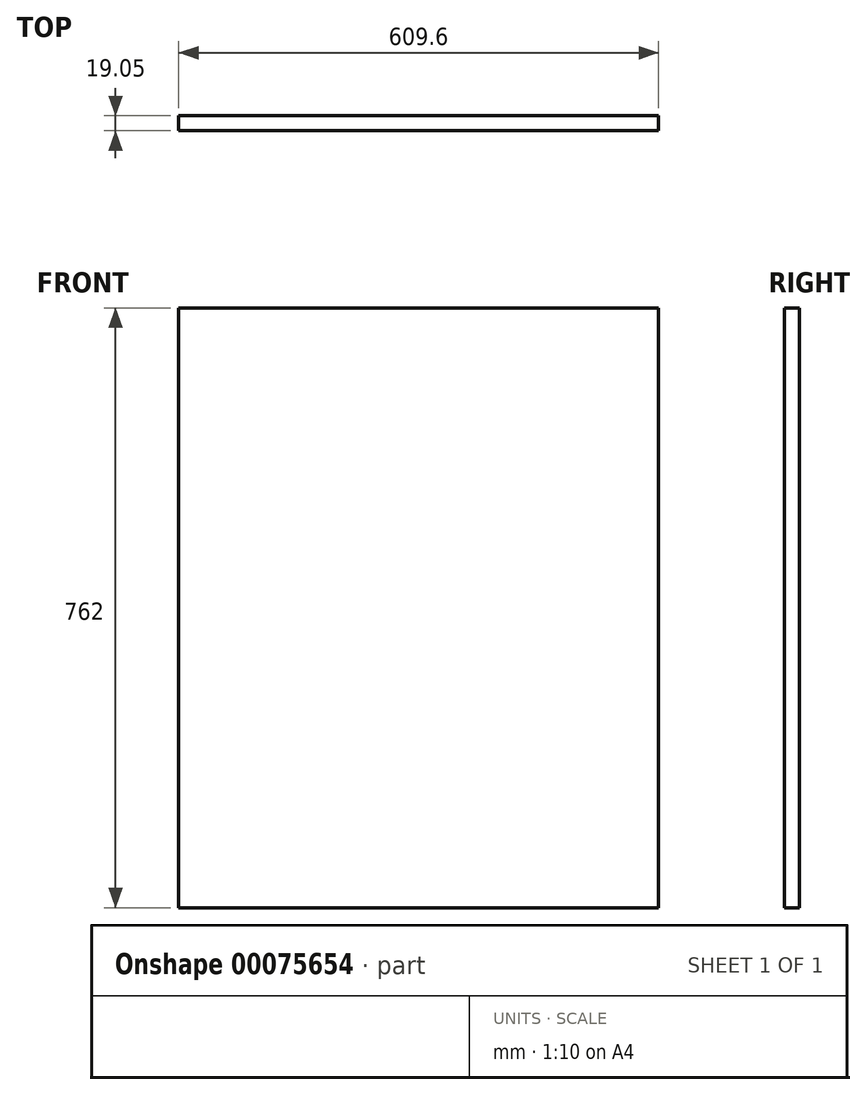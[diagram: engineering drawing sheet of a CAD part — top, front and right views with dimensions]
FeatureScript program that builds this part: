
annotation { "Feature Type Name" : "Feature", "Feature Type Description" : "" }
export const myFeature = defineFeature(function(context is Context, id is Id, definition is map)
    precondition{}
    {
        {
            var Q0;
            Q0=qCreatedBy(makeId("Front.planeOp"),FACE);
            var sketch = newSketch(context, id + "F0", { "sketchPlane" : qUnion([Q0])});
            skLineSegment(sketch, "E0.bottom", {"start": v(0, 0) * mm, "end": v(609.6, 0) * mm});
            skLineSegment(sketch, "E0.top", {"start": v(0, 762) * mm, "end": v(609.6, 762) * mm});
            skLineSegment(sketch, "E0.left", {"start": v(0, 0) * mm, "end": v(0, 762) * mm});
            skLineSegment(sketch, "E0.right", {"start": v(609.6, 0) * mm, "end": v(609.6, 762) * mm});
            skSolve(sketch);
        }
        {
            var Q0;
            Q0=makeQuery(id+"F0.imprint","IMPRINT",FACE,{"disambiguationData":[TD([[makeQuery(id+"F0.imprint","IMPRINT",EDGE,{"derivedFrom":sQuery(id+"F0.wireOp",EDGE,"E0.bottom")}),1.0]])]});
            extrude(context, id + "F1", {"entities" : qUnion([Q0]), "depth" : 19.05 * mm});
        }
    });
